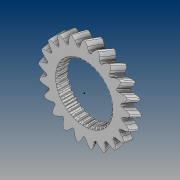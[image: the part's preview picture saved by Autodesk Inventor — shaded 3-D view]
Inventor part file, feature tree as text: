
AUTODESK INVENTOR PART (.ipt)
format: ipt  version: 2021 (Build 250183000, 183)  size: 1,553,920 bytes
history: native  units: mm
features: sketch x4, extrude x3, pattern_circular x3, fillet x3, helix x1
ambient origin geometry x8: Origin, YZ Plane, XZ Plane, XY Plane, X Axis, Y Axis, Z Axis, Center Point
bodies: Solid1 (feature_tree)
feature tree (14):
  extrude  "Extrusion1"  Depth=7.936mm
  helix  "Coil1"  [1 undecoded]
  pattern_circular  "Circular Pattern1"  [2 undecoded]
  sketch  "Sketch3"  dims[d14=80.0mm d15=0.0mm d16=0.0mm d17=0.0mm d18=0.0mm d19=74.0mm d22=14.3117mm d23=36.936003mm d24=2.175251mm d25=2.061732mm d26=11.285177mm]
  sketch  "Sketch4"  dims[d27=0.0mm d28=0.0mm d29=0.0mm d30=0.0mm d31=360.0mm d32=360.0deg d34=3.0mm d35=3.0mm d36=0.5mm d37=360.0mm d38=360.0deg]
  extrude  "Extrusion2"  Depth=0.5mm TaperAngle=360.0deg
  extrude  "Extrusion3"  Depth=0.5mm
  pattern_circular  "Circular Pattern2"  [2 undecoded]
  fillet  "Fillet1"  Radius=0.5mm
  fillet  "Fillet2"  Radius=360.0mm
  fillet  "Fillet3"  [1 undecoded]
  pattern_circular  "Circular Pattern3"  [2 undecoded]
  sketch  "Sketch1"  dims[d0=15.872mm d1=0.0mm d2=7.936mm]
  sketch  "Sketch2"  dims[d3=780.532359mm d4=15.872mm d5=10.0mm d6=0.0mm d7=0.0mm d8=0.0mm d9=0.0mm d10=0.0mm d11=210.0mm d12=2.991993mm]
note: 8 required parameter values undecoded (feature->parameter linkage not recoverable at this tier; creation-order binding heuristic only, values carry confidence <= 0.55)
